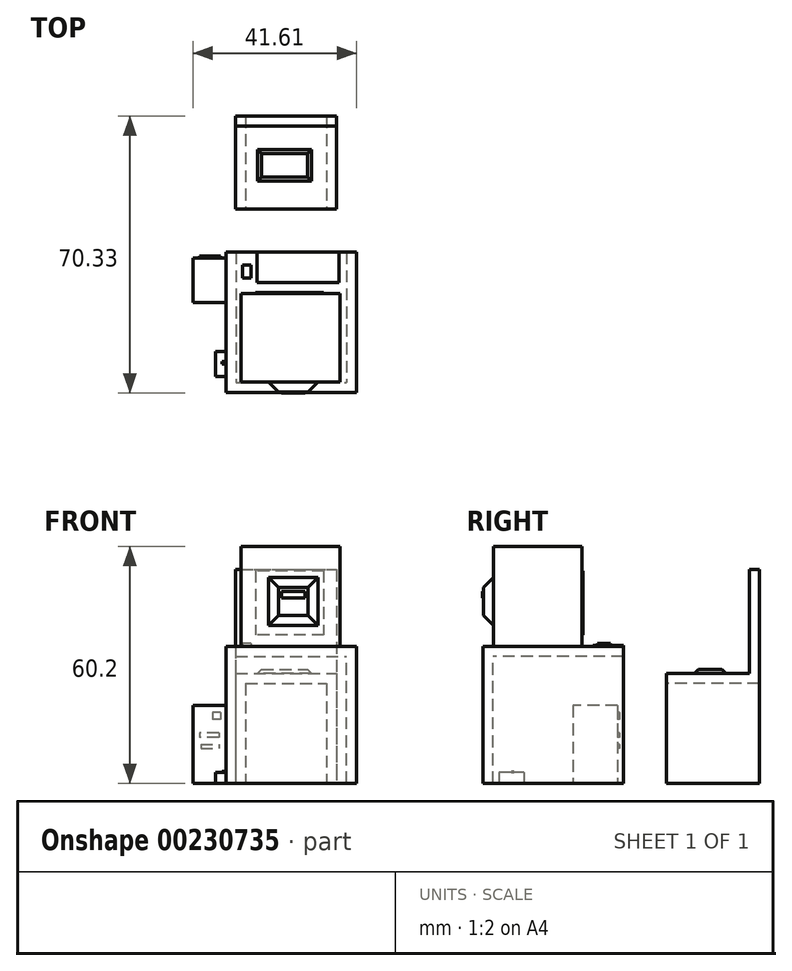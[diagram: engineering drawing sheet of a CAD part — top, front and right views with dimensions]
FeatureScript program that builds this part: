
annotation { "Feature Type Name" : "Feature", "Feature Type Description" : "" }
export const myFeature = defineFeature(function(context is Context, id is Id, definition is map)
    precondition{}
    {
        {
            var Q0;
            Q0=qCreatedBy(makeId("Front.planeOp"),FACE);
            var sketch = newSketch(context, id + "F0", { "sketchPlane" : qUnion([Q0])});
            skLineSegment(sketch, "E0.bottom", {"start": v(-33.72, 28.92) * mm, "end": v(-8.07, 28.92) * mm});
            skLineSegment(sketch, "E0.top", {"start": v(-33.72, 0) * mm, "end": v(-8.07, 0) * mm});
            skLineSegment(sketch, "E0.left", {"start": v(-33.72, 28.92) * mm, "end": v(-33.72, 0) * mm});
            skLineSegment(sketch, "E0.right", {"start": v(-8.07, 28.92) * mm, "end": v(-8.07, 0) * mm});
            skSolve(sketch);
        }
        {
            var Q0;
            Q0 = qSketchRegion(id + "F0", true);
            extrude(context, id + "F1", {"entities" : qUnion([Q0]), "oppositeDirection" : true, "depth" : 23.62 * mm});
        }
        {
            var Q0;
            Q0=makeQuery(id+"F1.opExtrude","SWEPT_FACE",FACE,{"disambiguationData":[OSD([sQuery(id+"F0.wireOp",EDGE,"E0.left")])]});
            var Q1;
            Q1=makeQuery(id+"F1.opExtrude","SWEPT_FACE",FACE,{"disambiguationData":[OSD([sQuery(id+"F0.wireOp",EDGE,"E0.bottom")])]});
            var Q2;
            Q2=makeQuery(id+"F1.opExtrude","CAP_FACE",FACE,{"disambiguationData":[OSD([sQuery(id+"F0.wireOp",EDGE,"E0.bottom"),sQuery(id+"F0.wireOp",EDGE,"E0.top"),sQuery(id+"F0.wireOp",EDGE,"E0.left"),sQuery(id+"F0.wireOp",EDGE,"E0.right")])],"isStart":true});
            var Q3;
            Q3=makeQuery(id+"F1.opExtrude","SWEPT_FACE",FACE,{"disambiguationData":[OSD([sQuery(id+"F0.wireOp",EDGE,"E0.right")])]});
            shell(context, id + "F2", {"entities" : qUnion([Q0, Q1, Q2, Q3]), "thickness" : 2.54 * mm});
        }
        {
            var Q0;
            Q0=makeQuery(id+"F1.opExtrude","SWEPT_FACE",FACE,{"disambiguationData":[OSD([sQuery(id+"F0.wireOp",EDGE,"E0.top")])]});
            extrude(context, id + "F3", {"entities" : qUnion([Q0]), "operationType" : NewBodyOperationType.ADD, "depth" : 25.4 * mm});
        }
        {
            var Q0;
            {var subQ0=sQuery(id+"F0.wireOp",EDGE,"E0.top");Q0=makeQuery(id+"F3.boolean.opBoolean","MERGE",FACE,{"derivedFrom":[makeQuery(id+"F1.opExtrude","CAP_FACE",FACE,{"disambiguationData":[OSD([sQuery(id+"F0.wireOp",EDGE,"E0.bottom"),subQ0,sQuery(id+"F0.wireOp",EDGE,"E0.left"),sQuery(id+"F0.wireOp",EDGE,"E0.right")])],"isStart":true}),makeQuery(id+"F3.opExtrude","SWEPT_FACE",FACE,{"disambiguationData":[OSD([subQ0]),TDD([makeQuery(id+"F1.opExtrude","CAP_EDGE",EDGE,{"disambiguationData":[OSD([subQ0])],"isStart":true})])]})]});}
            var Q1;
            Q1=makeQuery(id+"F3.opExtrude","CAP_FACE",FACE,{"disambiguationData":[OSD([sQuery(id+"F0.wireOp",EDGE,"E0.top")])],"isStart":false});
            var Q2;
            {var subQ0=sQuery(id+"F0.wireOp",EDGE,"E0.top");Q2=makeQuery(id+"F3.boolean.opBoolean","MERGE",FACE,{"derivedFrom":[makeQuery(id+"F1.opExtrude","CAP_FACE",FACE,{"disambiguationData":[OSD([sQuery(id+"F0.wireOp",EDGE,"E0.bottom"),subQ0,sQuery(id+"F0.wireOp",EDGE,"E0.left"),sQuery(id+"F0.wireOp",EDGE,"E0.right")])],"isStart":false}),makeQuery(id+"F3.opExtrude","SWEPT_FACE",FACE,{"disambiguationData":[OSD([subQ0]),TDD([makeQuery(id+"F1.opExtrude","CAP_EDGE",EDGE,{"disambiguationData":[OSD([subQ0])],"isStart":false})])]})]});}
            shell(context, id + "F4", {"entities" : qUnion([Q0, Q1, Q2]), "thickness" : 2.54 * mm});
        }
        {
            var Q0;
            Q0=qCreatedBy(makeId("Top.planeOp"),FACE);
            var sketch = newSketch(context, id + "F5", { "sketchPlane" : qUnion([Q0])});
            skLineSegment(sketch, "E1.bottom", {"start": v(-36.25, -10.96) * mm, "end": v(-3.02, -10.96) * mm});
            skLineSegment(sketch, "E1.top", {"start": v(-36.25, -46.63) * mm, "end": v(-3.02, -46.63) * mm});
            skLineSegment(sketch, "E1.left", {"start": v(-36.25, -10.96) * mm, "end": v(-36.25, -46.63) * mm});
            skLineSegment(sketch, "E1.right", {"start": v(-3.02, -10.96) * mm, "end": v(-3.02, -46.63) * mm});
            skSolve(sketch);
        }
        {
            var Q0;
            Q0 = qSketchRegion(id + "F5", true);
            extrude(context, id + "F6", {"entities" : qUnion([Q0]), "oppositeDirection" : true, "depth" : 25.4 * mm});
        }
        {
            var Q0;
            Q0=makeQuery(id+"F6.opExtrude","CAP_FACE",FACE,{"disambiguationData":[OSD([sQuery(id+"F5.wireOp",EDGE,"E1.bottom"),sQuery(id+"F5.wireOp",EDGE,"E1.top"),sQuery(id+"F5.wireOp",EDGE,"E1.left"),sQuery(id+"F5.wireOp",EDGE,"E1.right")])],"isStart":true});
            extrude(context, id + "F7", {"entities" : qUnion([Q0]), "operationType" : NewBodyOperationType.ADD, "depth" : 9.4 * mm});
        }
        {
            var Q0;
            Q0=makeQuery(id+"F6.opExtrude","CAP_FACE",FACE,{"disambiguationData":[OSD([sQuery(id+"F5.wireOp",EDGE,"E1.bottom"),sQuery(id+"F5.wireOp",EDGE,"E1.top"),sQuery(id+"F5.wireOp",EDGE,"E1.left"),sQuery(id+"F5.wireOp",EDGE,"E1.right")])],"isStart":false});
            var Q1;
            {var subQ0=sQuery(id+"F5.wireOp",EDGE,"E1.bottom");Q1=makeQuery(id+"F7.boolean.opBoolean","MERGE",FACE,{"derivedFrom":[makeQuery(id+"F6.opExtrude","SWEPT_FACE",FACE,{"disambiguationData":[OSD([subQ0])]}),makeQuery(id+"F7.opExtrude","SWEPT_FACE",FACE,{"disambiguationData":[OSD([subQ0])]})]});}
            shell(context, id + "F8", {"entities" : qUnion([Q0, Q1]), "thickness" : 2.54 * mm});
        }
        {
            var Q0;
            Q0=makeQuery(id+"F7.opExtrude","CAP_FACE",FACE,{"disambiguationData":[OSD([sQuery(id+"F5.wireOp",EDGE,"E1.bottom"),sQuery(id+"F5.wireOp",EDGE,"E1.top"),sQuery(id+"F5.wireOp",EDGE,"E1.left"),sQuery(id+"F5.wireOp",EDGE,"E1.right")])],"isStart":false});
            var sketch = newSketch(context, id + "F9", { "sketchPlane" : qUnion([Q0])});
            skLineSegment(sketch, "E2.bottom", {"start": v(-32.32, -21.45) * mm, "end": v(-7.26, -21.45) * mm});
            skLineSegment(sketch, "E2.top", {"start": v(-32.32, -43.91) * mm, "end": v(-7.26, -43.91) * mm});
            skLineSegment(sketch, "E2.left", {"start": v(-32.32, -21.45) * mm, "end": v(-32.32, -43.91) * mm});
            skLineSegment(sketch, "E2.right", {"start": v(-7.26, -21.45) * mm, "end": v(-7.26, -43.91) * mm});
            skSolve(sketch);
        }
        {
            var Q0;
            Q0 = qSketchRegion(id + "F9", true);
            extrude(context, id + "F10", {"entities" : qUnion([Q0]), "operationType" : NewBodyOperationType.ADD, "depth" : 25.4 * mm});
        }
        {
            var Q0;
            Q0=makeQuery(id+"F10.opExtrude","SWEPT_FACE",FACE,{"disambiguationData":[OSD([sQuery(id+"F9.wireOp",EDGE,"E2.bottom")])]});
            var sketch = newSketch(context, id + "F11", { "sketchPlane" : qUnion([Q0])});
            skLineSegment(sketch, "E3.bottom", {"start": v(11.38, 28.6) * mm, "end": v(28.75, 28.6) * mm});
            skLineSegment(sketch, "E3.top", {"start": v(11.38, 12.36) * mm, "end": v(28.75, 12.36) * mm});
            skLineSegment(sketch, "E3.left", {"start": v(11.38, 28.6) * mm, "end": v(11.38, 12.36) * mm});
            skLineSegment(sketch, "E3.right", {"start": v(28.75, 28.6) * mm, "end": v(28.75, 12.36) * mm});
            skSolve(sketch);
        }
        {
            var Q0;
            Q0 = qSketchRegion(id + "F11", true);
            extrude(context, id + "F12", {"entities" : qUnion([Q0]), "operationType" : NewBodyOperationType.ADD, "depth" : 0.25 * mm});
        }
        {
            var Q0;
            Q0=makeQuery(id+"F7.opExtrude","CAP_FACE",FACE,{"disambiguationData":[OSD([sQuery(id+"F5.wireOp",EDGE,"E1.bottom"),sQuery(id+"F5.wireOp",EDGE,"E1.top"),sQuery(id+"F5.wireOp",EDGE,"E1.left"),sQuery(id+"F5.wireOp",EDGE,"E1.right")])],"isStart":false});
            var sketch = newSketch(context, id + "F13", { "sketchPlane" : qUnion([Q0])});
            skLineSegment(sketch, "E4.bottom", {"start": v(-7.44, -18.67) * mm, "end": v(-28.3, -18.67) * mm});
            skLineSegment(sketch, "E4.top", {"start": v(-7.44, -10.96) * mm, "end": v(-28.3, -10.96) * mm});
            skLineSegment(sketch, "E4.left", {"start": v(-7.44, -18.67) * mm, "end": v(-7.44, -10.96) * mm});
            skLineSegment(sketch, "E4.right", {"start": v(-28.3, -18.67) * mm, "end": v(-28.3, -10.96) * mm});
            skSolve(sketch);
        }
        {
            var Q0;
            Q0 = qSketchRegion(id + "F13", true);
            extrude(context, id + "F14", {"entities" : qUnion([Q0]), "operationType" : NewBodyOperationType.ADD, "depth" : 0.25 * mm});
        }
        {
            var Q0;
            Q0=makeQuery(id+"F10.opExtrude","SWEPT_FACE",FACE,{"disambiguationData":[OSD([sQuery(id+"F9.wireOp",EDGE,"E2.top")])]});
            var sketch = newSketch(context, id + "F15", { "sketchPlane" : qUnion([Q0])});
            skLineSegment(sketch, "E5.bottom", {"start": v(-27.92, 29.49) * mm, "end": v(-10.34, 29.49) * mm});
            skLineSegment(sketch, "E5.top", {"start": v(-27.92, 12.17) * mm, "end": v(-10.34, 12.17) * mm});
            skLineSegment(sketch, "E5.left", {"start": v(-27.92, 29.49) * mm, "end": v(-27.92, 12.17) * mm});
            skLineSegment(sketch, "E5.right", {"start": v(-10.34, 29.49) * mm, "end": v(-10.34, 12.17) * mm});
            skSolve(sketch);
        }
        {
            var Q0;
            Q0 = qSketchRegion(id + "F15", true);
            extrude(context, id + "F16", {"entities" : qUnion([Q0]), "operationType" : NewBodyOperationType.ADD, "depth" : 2.54 * mm});
        }
        {
            var Q0;
            Q0=makeQuery(id+"F16.opExtrude","CAP_FACE",FACE,{"disambiguationData":[OSD([sQuery(id+"F15.wireOp",EDGE,"E5.bottom"),sQuery(id+"F15.wireOp",EDGE,"E5.top"),sQuery(id+"F15.wireOp",EDGE,"E5.left"),sQuery(id+"F15.wireOp",EDGE,"E5.right")])],"isStart":false});
            chamfer(context, id + "F17", {"entities" : qUnion([Q0]), "width" : 5.08 * mm, "tangentPropagation" : true});
        }
        {
            var Q0;
            Q0=makeQuery(id+"F16.opExtrude","CAP_FACE",FACE,{"disambiguationData":[OSD([sQuery(id+"F15.wireOp",EDGE,"E5.bottom"),sQuery(id+"F15.wireOp",EDGE,"E5.top"),sQuery(id+"F15.wireOp",EDGE,"E5.left"),sQuery(id+"F15.wireOp",EDGE,"E5.right")])],"isStart":false});
            var sketch = newSketch(context, id + "F18", { "sketchPlane" : qUnion([Q0])});
            skLineSegment(sketch, "E6.bottom", {"start": v(-22.16, 23.41) * mm, "end": v(-16.16, 23.41) * mm});
            skLineSegment(sketch, "E6.top", {"start": v(-22.16, 21.76) * mm, "end": v(-16.16, 21.76) * mm});
            skLineSegment(sketch, "E6.left", {"start": v(-22.16, 23.41) * mm, "end": v(-22.16, 21.76) * mm});
            skLineSegment(sketch, "E6.right", {"start": v(-16.16, 23.41) * mm, "end": v(-16.16, 21.76) * mm});
            skSolve(sketch);
        }
        {
            var Q0;
            Q0 = qSketchRegion(id + "F18", true);
            extrude(context, id + "F19", {"entities" : qUnion([Q0]), "operationType" : NewBodyOperationType.ADD, "depth" : 0.25 * mm});
        }
        {
            var Q0;
            Q0=makeQuery(id+"F7.opExtrude","CAP_FACE",FACE,{"disambiguationData":[OSD([sQuery(id+"F5.wireOp",EDGE,"E1.bottom"),sQuery(id+"F5.wireOp",EDGE,"E1.top"),sQuery(id+"F5.wireOp",EDGE,"E1.left"),sQuery(id+"F5.wireOp",EDGE,"E1.right")])],"isStart":false});
            var sketch = newSketch(context, id + "F20", { "sketchPlane" : qUnion([Q0])});
            skLineSegment(sketch, "E7.bottom", {"start": v(-29.82, -17.48) * mm, "end": v(-32, -17.48) * mm});
            skLineSegment(sketch, "E7.top", {"start": v(-29.82, -14.22) * mm, "end": v(-32, -14.22) * mm});
            skLineSegment(sketch, "E7.left", {"start": v(-29.82, -17.48) * mm, "end": v(-29.82, -14.22) * mm});
            skLineSegment(sketch, "E7.right", {"start": v(-32, -17.48) * mm, "end": v(-32, -14.22) * mm});
            skSolve(sketch);
        }
        {
            var Q0;
            Q0 = qSketchRegion(id + "F20", true);
            extrude(context, id + "F21", {"entities" : qUnion([Q0]), "operationType" : NewBodyOperationType.ADD, "depth" : 0.76 * mm});
        }
        {
            var Q0;
            Q0=makeQuery(id+"F2.opShell","OFFSET_FACE",FACE,{"disambiguationData":[OSD([sQuery(id+"F0.wireOp",EDGE,"E0.top")])]});
            var sketch = newSketch(context, id + "F22", { "sketchPlane" : qUnion([Q0])});
            skLineSegment(sketch, "E8.bottom", {"start": v(-32.22, 19.2) * mm, "end": v(-10.4, 19.2) * mm});
            skLineSegment(sketch, "E8.top", {"start": v(-32.22, 3.02) * mm, "end": v(-10.4, 3.02) * mm});
            skLineSegment(sketch, "E8.left", {"start": v(-32.22, 19.2) * mm, "end": v(-32.22, 3.02) * mm});
            skLineSegment(sketch, "E8.right", {"start": v(-10.4, 19.2) * mm, "end": v(-10.4, 3.02) * mm});
            skSolve(sketch);
        }
        {
            var Q0;
            Q0 = qSketchRegion(id + "F22", true);
            extrude(context, id + "F23", {"entities" : qUnion([Q0]), "operationType" : NewBodyOperationType.ADD, "depth" : 1.02 * mm});
        }
        {
            var Q0;
            {var subQ0=sQuery(id+"F5.wireOp",EDGE,"E1.left");Q0=makeQuery(id+"F7.boolean.opBoolean","MERGE",FACE,{"derivedFrom":[makeQuery(id+"F6.opExtrude","SWEPT_FACE",FACE,{"disambiguationData":[OSD([subQ0])]}),makeQuery(id+"F7.opExtrude","SWEPT_FACE",FACE,{"disambiguationData":[OSD([subQ0])]})]});}
            var sketch = newSketch(context, id + "F24", { "sketchPlane" : qUnion([Q0])});
            skLineSegment(sketch, "E9.bottom", {"start": v(12.47, -5.63) * mm, "end": v(23.7, -5.63) * mm});
            skLineSegment(sketch, "E9.top", {"start": v(12.47, -25.4) * mm, "end": v(23.7, -25.4) * mm});
            skLineSegment(sketch, "E9.left", {"start": v(12.47, -5.63) * mm, "end": v(12.47, -25.4) * mm});
            skLineSegment(sketch, "E9.right", {"start": v(23.7, -5.63) * mm, "end": v(23.7, -25.4) * mm});
            skSolve(sketch);
        }
        {
            var Q0;
            Q0 = qSketchRegion(id + "F24", true);
            extrude(context, id + "F25", {"entities" : qUnion([Q0]), "operationType" : NewBodyOperationType.ADD, "depth" : 8.38 * mm});
        }
        {
            var Q0;
            Q0=makeQuery(id+"F25.opExtrude","SWEPT_FACE",FACE,{"disambiguationData":[OSD([sQuery(id+"F24.wireOp",EDGE,"E9.left")])]});
            var sketch = newSketch(context, id + "F26", { "sketchPlane" : qUnion([Q0])});
            skLineSegment(sketch, "E10.bottom", {"start": v(37.6, -7.36) * mm, "end": v(39.62, -7.36) * mm});
            skLineSegment(sketch, "E10.top", {"start": v(37.6, -9.2) * mm, "end": v(39.62, -9.2) * mm});
            skLineSegment(sketch, "E10.left", {"start": v(37.6, -7.36) * mm, "end": v(37.6, -9.2) * mm});
            skLineSegment(sketch, "E10.right", {"start": v(39.62, -7.36) * mm, "end": v(39.62, -9.2) * mm});
            skSolve(sketch);
        }
        {
            var Q0;
            Q0 = qSketchRegion(id + "F26", true);
            extrude(context, id + "F27", {"entities" : qUnion([Q0]), "operationType" : NewBodyOperationType.ADD, "depth" : 0.5 * mm});
        }
        {
            var Q0;
            Q0=makeQuery(id+"F25.opExtrude","SWEPT_FACE",FACE,{"disambiguationData":[OSD([sQuery(id+"F24.wireOp",EDGE,"E9.left")])]});
            var sketch = newSketch(context, id + "F28", { "sketchPlane" : qUnion([Q0])});
            skLineSegment(sketch, "E11.bottom", {"start": v(37.98, -12.62) * mm, "end": v(42.9, -12.62) * mm});
            skLineSegment(sketch, "E11.top", {"start": v(37.98, -13.78) * mm, "end": v(42.9, -13.78) * mm});
            skLineSegment(sketch, "E11.left", {"start": v(37.98, -12.62) * mm, "end": v(37.98, -13.78) * mm});
            skLineSegment(sketch, "E11.right", {"start": v(42.9, -12.62) * mm, "end": v(42.9, -13.78) * mm});
            skSolve(sketch);
        }
        {
            var Q0;
            Q0 = qSketchRegion(id + "F28", true);
            extrude(context, id + "F29", {"entities" : qUnion([Q0]), "operationType" : NewBodyOperationType.ADD, "depth" : 0.5 * mm});
        }
        {
            var Q0;
            Q0=makeQuery(id+"F25.opExtrude","SWEPT_FACE",FACE,{"disambiguationData":[OSD([sQuery(id+"F24.wireOp",EDGE,"E9.left")])]});
            var sketch = newSketch(context, id + "F30", { "sketchPlane" : qUnion([Q0])});
            skPoint(sketch, "E12.firstSnap0", {"position": v(36.25, -15.51) * mm});
            skLineSegment(sketch, "E12.bottom", {"start": v(42.56, -15.51) * mm, "end": v(37.98, -15.51) * mm});
            skLineSegment(sketch, "E12.top", {"start": v(42.56, -16.47) * mm, "end": v(37.98, -16.47) * mm});
            skLineSegment(sketch, "E12.left", {"start": v(42.56, -15.51) * mm, "end": v(42.56, -16.47) * mm});
            skLineSegment(sketch, "E12.right", {"start": v(37.98, -15.51) * mm, "end": v(37.98, -16.47) * mm});
            skSolve(sketch);
        }
        {
            var Q0;
            Q0 = qSketchRegion(id + "F30", true);
            extrude(context, id + "F31", {"entities" : qUnion([Q0]), "operationType" : NewBodyOperationType.ADD, "depth" : 0.5 * mm});
        }
        {
            var Q0;
            {var subQ0=sQuery(id+"F5.wireOp",EDGE,"E1.left");Q0=makeQuery(id+"F7.boolean.opBoolean","MERGE",FACE,{"derivedFrom":[makeQuery(id+"F6.opExtrude","SWEPT_FACE",FACE,{"disambiguationData":[OSD([subQ0])]}),makeQuery(id+"F7.opExtrude","SWEPT_FACE",FACE,{"disambiguationData":[OSD([subQ0])]})]});}
            var sketch = newSketch(context, id + "F32", { "sketchPlane" : qUnion([Q0])});
            skLineSegment(sketch, "E13.bottom", {"start": v(36.21, -22.57) * mm, "end": v(42.53, -22.57) * mm});
            skLineSegment(sketch, "E13.top", {"start": v(36.21, -25.4) * mm, "end": v(42.53, -25.4) * mm});
            skLineSegment(sketch, "E13.left", {"start": v(36.21, -22.57) * mm, "end": v(36.21, -25.4) * mm});
            skLineSegment(sketch, "E13.right", {"start": v(42.53, -22.57) * mm, "end": v(42.53, -25.4) * mm});
            skSolve(sketch);
        }
        {
            var Q0;
            Q0 = qSketchRegion(id + "F32", true);
            extrude(context, id + "F33", {"entities" : qUnion([Q0]), "operationType" : NewBodyOperationType.ADD, "depth" : 2.62 * mm});
        }
        {
            var Q0;
            Q0=makeQuery(id+"F33.opExtrude","SWEPT_FACE",FACE,{"disambiguationData":[OSD([sQuery(id+"F32.wireOp",EDGE,"E13.bottom")])]});
            var sketch = newSketch(context, id + "F34", { "sketchPlane" : qUnion([Q0])});
            skLineSegment(sketch, "E14.bottom", {"start": v(-36.25, -39.37) * mm, "end": v(-37.2, -39.37) * mm});
            skLineSegment(sketch, "E14.top", {"start": v(-36.25, -38.71) * mm, "end": v(-37.2, -38.71) * mm});
            skLineSegment(sketch, "E14.left", {"start": v(-36.25, -39.37) * mm, "end": v(-36.25, -38.71) * mm});
            skLineSegment(sketch, "E14.right", {"start": v(-37.2, -39.37) * mm, "end": v(-37.2, -38.71) * mm});
            skSolve(sketch);
        }
        {
            var Q0;
            Q0 = qSketchRegion(id + "F34", true);
            extrude(context, id + "F35", {"entities" : qUnion([Q0]), "operationType" : NewBodyOperationType.ADD, "depth" : 0.2 * mm});
        }
        {
            var Q0;
            Q0=makeQuery(id+"F23.opExtrude","CAP_FACE",FACE,{"disambiguationData":[OSD([sQuery(id+"F22.wireOp",EDGE,"E8.bottom"),sQuery(id+"F22.wireOp",EDGE,"E8.top"),sQuery(id+"F22.wireOp",EDGE,"E8.left"),sQuery(id+"F22.wireOp",EDGE,"E8.right")])],"isStart":false});
            chamfer(context, id + "F36", {"entities" : qUnion([Q0]), "width" : 5.08 * mm, "tangentPropagation" : true});
        }
        {
            var Q0;
            Q0=qCreatedBy(makeId("Top.planeOp"),FACE);
            var sketch = newSketch(context, id + "F37", { "sketchPlane" : qUnion([Q0])});
            skLineSegment(sketch, "E15.bottom", {"start": v(-47.78, -38) * mm, "end": v(-48.77, -38) * mm});
            skLineSegment(sketch, "E15.top", {"start": v(-47.78, -38.6) * mm, "end": v(-48.77, -38.6) * mm});
            skLineSegment(sketch, "E15.left", {"start": v(-47.78, -38) * mm, "end": v(-47.78, -38.6) * mm});
            skLineSegment(sketch, "E15.right", {"start": v(-48.77, -38) * mm, "end": v(-48.77, -38.6) * mm});
            skLineSegment(sketch, "E16.bottom", {"start": v(-46.74, -37.18) * mm, "end": v(-47.47, -37.18) * mm});
            skLineSegment(sketch, "E16.top", {"start": v(-46.74, -37.7) * mm, "end": v(-47.47, -37.7) * mm});
            skLineSegment(sketch, "E16.left", {"start": v(-46.74, -37.18) * mm, "end": v(-46.74, -37.7) * mm});
            skLineSegment(sketch, "E16.right", {"start": v(-47.47, -37.18) * mm, "end": v(-47.47, -37.7) * mm});
            skLineSegment(sketch, "E17.bottom", {"start": v(-47.66, -37.09) * mm, "end": v(-48.8, -37.09) * mm});
            skLineSegment(sketch, "E17.top", {"start": v(-47.66, -37.77) * mm, "end": v(-48.8, -37.77) * mm});
            skLineSegment(sketch, "E17.left", {"start": v(-47.66, -37.09) * mm, "end": v(-47.66, -37.77) * mm});
            skLineSegment(sketch, "E17.right", {"start": v(-48.8, -37.09) * mm, "end": v(-48.8, -37.77) * mm});
            skLineSegment(sketch, "E18.bottom", {"start": v(-46.74, -36.38) * mm, "end": v(-47.47, -36.38) * mm});
            skLineSegment(sketch, "E18.top", {"start": v(-46.74, -36.92) * mm, "end": v(-47.47, -36.92) * mm});
            skLineSegment(sketch, "E18.left", {"start": v(-46.74, -36.38) * mm, "end": v(-46.74, -36.92) * mm});
            skLineSegment(sketch, "E18.right", {"start": v(-47.47, -36.38) * mm, "end": v(-47.47, -36.92) * mm});
            skLineSegment(sketch, "E19.bottom", {"start": v(-47.57, -36.4) * mm, "end": v(-48.85, -36.4) * mm});
            skLineSegment(sketch, "E19.top", {"start": v(-47.57, -36.89) * mm, "end": v(-48.85, -36.89) * mm});
            skLineSegment(sketch, "E19.left", {"start": v(-47.57, -36.4) * mm, "end": v(-47.57, -36.89) * mm});
            skLineSegment(sketch, "E19.right", {"start": v(-48.85, -36.4) * mm, "end": v(-48.85, -36.89) * mm});
            skLineSegment(sketch, "E20.bottom", {"start": v(-46.8, -35.65) * mm, "end": v(-47.5, -35.65) * mm});
            skLineSegment(sketch, "E20.top", {"start": v(-46.8, -36.21) * mm, "end": v(-47.5, -36.21) * mm});
            skLineSegment(sketch, "E20.left", {"start": v(-46.8, -35.65) * mm, "end": v(-46.8, -36.21) * mm});
            skLineSegment(sketch, "E20.right", {"start": v(-47.5, -35.65) * mm, "end": v(-47.5, -36.21) * mm});
            skLineSegment(sketch, "E21.bottom", {"start": v(-47.8, -35.75) * mm, "end": v(-48.87, -35.75) * mm});
            skLineSegment(sketch, "E21.top", {"start": v(-47.8, -36.24) * mm, "end": v(-48.87, -36.24) * mm});
            skLineSegment(sketch, "E21.left", {"start": v(-47.8, -35.75) * mm, "end": v(-47.8, -36.24) * mm});
            skLineSegment(sketch, "E21.right", {"start": v(-48.87, -35.75) * mm, "end": v(-48.87, -36.24) * mm});
            skLineSegment(sketch, "E22.bottom", {"start": v(-46.88, -38.9) * mm, "end": v(-47.5, -38.9) * mm});
            skLineSegment(sketch, "E22.top", {"start": v(-46.88, -39.32) * mm, "end": v(-47.5, -39.32) * mm});
            skLineSegment(sketch, "E22.left", {"start": v(-46.88, -38.9) * mm, "end": v(-46.88, -39.32) * mm});
            skLineSegment(sketch, "E22.right", {"start": v(-47.5, -38.9) * mm, "end": v(-47.5, -39.32) * mm});
            skLineSegment(sketch, "E23.bottom", {"start": v(-47.82, -38.6) * mm, "end": v(-48.66, -38.6) * mm});
            skLineSegment(sketch, "E23.top", {"start": v(-47.82, -39.43) * mm, "end": v(-48.66, -39.43) * mm});
            skLineSegment(sketch, "E23.left", {"start": v(-47.82, -38.6) * mm, "end": v(-47.82, -39.43) * mm});
            skLineSegment(sketch, "E23.right", {"start": v(-48.66, -38.6) * mm, "end": v(-48.66, -39.43) * mm});
            skLineSegment(sketch, "E24.bottom", {"start": v(-46.88, -39.7) * mm, "end": v(-47.66, -39.7) * mm});
            skLineSegment(sketch, "E24.top", {"start": v(-46.88, -40.17) * mm, "end": v(-47.66, -40.17) * mm});
            skLineSegment(sketch, "E24.left", {"start": v(-46.88, -39.7) * mm, "end": v(-46.88, -40.17) * mm});
            skLineSegment(sketch, "E24.right", {"start": v(-47.66, -39.7) * mm, "end": v(-47.66, -40.17) * mm});
            skLineSegment(sketch, "E25.bottom", {"start": v(-47.87, -39.71) * mm, "end": v(-48.94, -39.71) * mm});
            skLineSegment(sketch, "E25.top", {"start": v(-47.87, -40.31) * mm, "end": v(-48.94, -40.31) * mm});
            skLineSegment(sketch, "E25.left", {"start": v(-47.87, -39.71) * mm, "end": v(-47.87, -40.31) * mm});
            skLineSegment(sketch, "E25.right", {"start": v(-48.94, -39.71) * mm, "end": v(-48.94, -40.31) * mm});
            skLineSegment(sketch, "E26.bottom", {"start": v(-46.87, -40.5) * mm, "end": v(-48.02, -40.5) * mm});
            skLineSegment(sketch, "E26.top", {"start": v(-46.87, -40.87) * mm, "end": v(-48.02, -40.87) * mm});
            skLineSegment(sketch, "E26.left", {"start": v(-46.87, -40.5) * mm, "end": v(-46.87, -40.87) * mm});
            skLineSegment(sketch, "E26.right", {"start": v(-48.02, -40.5) * mm, "end": v(-48.02, -40.87) * mm});
            skLineSegment(sketch, "E27.bottom", {"start": v(-48.08, -40.6) * mm, "end": v(-48.94, -40.6) * mm});
            skLineSegment(sketch, "E27.top", {"start": v(-48.08, -40.97) * mm, "end": v(-48.94, -40.97) * mm});
            skLineSegment(sketch, "E27.left", {"start": v(-48.08, -40.6) * mm, "end": v(-48.08, -40.97) * mm});
            skLineSegment(sketch, "E27.right", {"start": v(-48.94, -40.6) * mm, "end": v(-48.94, -40.97) * mm});
            skLineSegment(sketch, "E28.bottom", {"start": v(-47.57, -41.22) * mm, "end": v(-46.82, -41.22) * mm});
            skLineSegment(sketch, "E28.top", {"start": v(-47.57, -41.75) * mm, "end": v(-46.82, -41.75) * mm});
            skLineSegment(sketch, "E28.left", {"start": v(-47.57, -41.22) * mm, "end": v(-47.57, -41.75) * mm});
            skLineSegment(sketch, "E28.right", {"start": v(-46.82, -41.22) * mm, "end": v(-46.82, -41.75) * mm});
            skLineSegment(sketch, "E29.bottom", {"start": v(-47.97, -41.32) * mm, "end": v(-49.05, -41.32) * mm});
            skLineSegment(sketch, "E29.top", {"start": v(-47.97, -41.85) * mm, "end": v(-49.05, -41.85) * mm});
            skLineSegment(sketch, "E29.left", {"start": v(-47.97, -41.32) * mm, "end": v(-47.97, -41.85) * mm});
            skLineSegment(sketch, "E29.right", {"start": v(-49.05, -41.32) * mm, "end": v(-49.05, -41.85) * mm});
            skSolve(sketch);
        }
        {
            var Q0;
            Q0 = qSketchRegion(id + "F37", true);
            extrude(context, id + "F38", {"entities" : qUnion([Q0]), "depth" : 0.5 * mm});
        }
        {
            var Q0;
            Q0=makeQuery(id+"F38.opExtrude","SWEPT_BODY",BODY,{"disambiguationData":[OSD([sQuery(id+"F37.wireOp",EDGE,"E29.bottom"),sQuery(id+"F37.wireOp",EDGE,"E29.top"),sQuery(id+"F37.wireOp",EDGE,"E29.left"),sQuery(id+"F37.wireOp",EDGE,"E29.right")])]});
            var Q1;
            Q1=makeQuery(id+"F38.opExtrude","SWEPT_BODY",BODY,{"disambiguationData":[OSD([sQuery(id+"F37.wireOp",EDGE,"E28.bottom"),sQuery(id+"F37.wireOp",EDGE,"E28.top"),sQuery(id+"F37.wireOp",EDGE,"E28.left"),sQuery(id+"F37.wireOp",EDGE,"E28.right")])]});
            var Q2;
            Q2=makeQuery(id+"F38.opExtrude","SWEPT_BODY",BODY,{"disambiguationData":[OSD([sQuery(id+"F37.wireOp",EDGE,"E27.bottom"),sQuery(id+"F37.wireOp",EDGE,"E27.top"),sQuery(id+"F37.wireOp",EDGE,"E27.left"),sQuery(id+"F37.wireOp",EDGE,"E27.right")])]});
            var Q3;
            Q3=makeQuery(id+"F38.opExtrude","SWEPT_BODY",BODY,{"disambiguationData":[OSD([sQuery(id+"F37.wireOp",EDGE,"E26.bottom"),sQuery(id+"F37.wireOp",EDGE,"E26.top"),sQuery(id+"F37.wireOp",EDGE,"E26.left"),sQuery(id+"F37.wireOp",EDGE,"E26.right")])]});
            var Q4;
            Q4=makeQuery(id+"F38.opExtrude","SWEPT_BODY",BODY,{"disambiguationData":[OSD([sQuery(id+"F37.wireOp",EDGE,"E25.bottom"),sQuery(id+"F37.wireOp",EDGE,"E25.top"),sQuery(id+"F37.wireOp",EDGE,"E25.left"),sQuery(id+"F37.wireOp",EDGE,"E25.right")])]});
            var Q5;
            Q5=makeQuery(id+"F38.opExtrude","SWEPT_BODY",BODY,{"disambiguationData":[OSD([sQuery(id+"F37.wireOp",EDGE,"E24.bottom"),sQuery(id+"F37.wireOp",EDGE,"E24.top"),sQuery(id+"F37.wireOp",EDGE,"E24.left"),sQuery(id+"F37.wireOp",EDGE,"E24.right")])]});
            var Q6;
            Q6=makeQuery(id+"F38.opExtrude","SWEPT_BODY",BODY,{"disambiguationData":[OSD([sQuery(id+"F37.wireOp",EDGE,"E22.bottom"),sQuery(id+"F37.wireOp",EDGE,"E22.top"),sQuery(id+"F37.wireOp",EDGE,"E22.left"),sQuery(id+"F37.wireOp",EDGE,"E22.right")])]});
            var Q7;
            Q7=makeQuery(id+"F38.opExtrude","SWEPT_BODY",BODY,{"disambiguationData":[OSD([sQuery(id+"F37.wireOp",EDGE,"E21.bottom"),sQuery(id+"F37.wireOp",EDGE,"E21.top"),sQuery(id+"F37.wireOp",EDGE,"E21.left"),sQuery(id+"F37.wireOp",EDGE,"E21.right")])]});
            var Q8;
            Q8=makeQuery(id+"F38.opExtrude","SWEPT_BODY",BODY,{"disambiguationData":[OSD([sQuery(id+"F37.wireOp",EDGE,"E20.bottom"),sQuery(id+"F37.wireOp",EDGE,"E20.top"),sQuery(id+"F37.wireOp",EDGE,"E20.left"),sQuery(id+"F37.wireOp",EDGE,"E20.right")])]});
            var Q9;
            Q9=makeQuery(id+"F38.opExtrude","SWEPT_BODY",BODY,{"disambiguationData":[OSD([sQuery(id+"F37.wireOp",EDGE,"E19.bottom"),sQuery(id+"F37.wireOp",EDGE,"E19.top"),sQuery(id+"F37.wireOp",EDGE,"E19.left"),sQuery(id+"F37.wireOp",EDGE,"E19.right")])]});
            var Q10;
            Q10=makeQuery(id+"F38.opExtrude","SWEPT_BODY",BODY,{"disambiguationData":[OSD([sQuery(id+"F37.wireOp",EDGE,"E18.bottom"),sQuery(id+"F37.wireOp",EDGE,"E18.top"),sQuery(id+"F37.wireOp",EDGE,"E18.left"),sQuery(id+"F37.wireOp",EDGE,"E18.right")])]});
            var Q11;
            Q11=makeQuery(id+"F38.opExtrude","SWEPT_BODY",BODY,{"disambiguationData":[OSD([sQuery(id+"F37.wireOp",EDGE,"E17.bottom"),sQuery(id+"F37.wireOp",EDGE,"E17.top"),sQuery(id+"F37.wireOp",EDGE,"E17.left"),sQuery(id+"F37.wireOp",EDGE,"E17.right")])]});
            var Q12;
            Q12=makeQuery(id+"F38.opExtrude","SWEPT_BODY",BODY,{"disambiguationData":[OSD([sQuery(id+"F37.wireOp",EDGE,"E16.bottom"),sQuery(id+"F37.wireOp",EDGE,"E16.top"),sQuery(id+"F37.wireOp",EDGE,"E16.left"),sQuery(id+"F37.wireOp",EDGE,"E16.right")])]});
            var Q13;
            Q13=makeQuery(id+"F38.opExtrude","SWEPT_BODY",BODY,{"disambiguationData":[OSD([sQuery(id+"F37.wireOp",EDGE,"E15.bottom"),sQuery(id+"F37.wireOp",EDGE,"E15.top"),sQuery(id+"F37.wireOp",EDGE,"E15.left"),sQuery(id+"F37.wireOp",EDGE,"E15.right"),sQuery(id+"F37.wireOp",EDGE,"E23.top"),sQuery(id+"F37.wireOp",EDGE,"E23.left"),sQuery(id+"F37.wireOp",EDGE,"E23.right")])]});
            deleteBodies(context, id + "F39", {"entities" : qUnion([Q0, Q1, Q2, Q3, Q4, Q5, Q6, Q7, Q8, Q9, Q10, Q11, Q12, Q13])});
        }
    });
